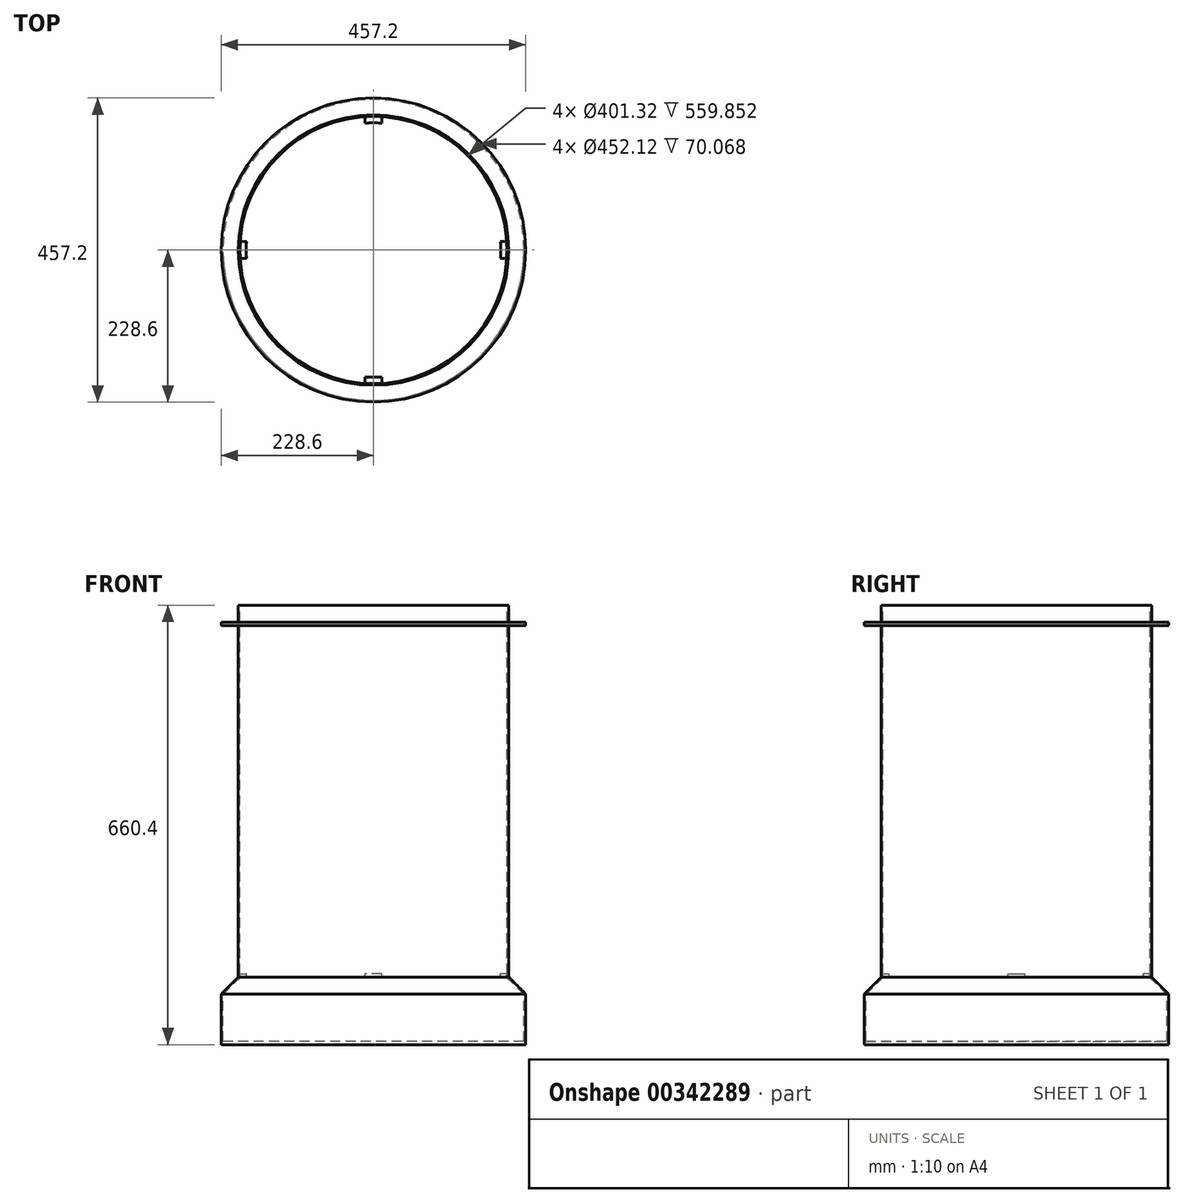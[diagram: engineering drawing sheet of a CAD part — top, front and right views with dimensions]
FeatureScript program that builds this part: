
annotation { "Feature Type Name" : "Feature", "Feature Type Description" : "" }
export const myFeature = defineFeature(function(context is Context, id is Id, definition is map)
    precondition{}
    {
        {
            var Q0;
            Q0=qCreatedBy(makeId("Front.planeOp"),FACE);
            var sketch = newSketch(context, id + "F0", { "sketchPlane" : qUnion([Q0])});
            skLineSegment(sketch, "E0", {"start": v(0, 0) * mm, "end": v(228.6, 0) * mm});
            skLineSegment(sketch, "E1", {"start": v(228.6, 0) * mm, "end": v(228.6, 76.2) * mm});
            skLineSegment(sketch, "E2", {"start": v(228.6, 76.2) * mm, "end": v(203.2, 101.6) * mm});
            skLineSegment(sketch, "E3", {"start": v(203.2, 101.6) * mm, "end": v(203.2, 629.92) * mm});
            skLineSegment(sketch, "E4", {"start": v(203.2, 629.92) * mm, "end": v(228.6, 629.92) * mm});
            skLineSegment(sketch, "E5", {"start": v(228.6, 629.92) * mm, "end": v(228.6, 635) * mm});
            skLineSegment(sketch, "E6", {"start": v(228.6, 635) * mm, "end": v(203.2, 635) * mm});
            skLineSegment(sketch, "E7", {"start": v(203.2, 635) * mm, "end": v(203.2, 660.4) * mm});
            skLineSegment(sketch, "E8", {"start": v(203.2, 660.4) * mm, "end": v(200.66, 660.4) * mm});
            skLineSegment(sketch, "E9", {"start": v(200.66, 660.4) * mm, "end": v(200.66, 106.68) * mm});
            skLineSegment(sketch, "E10", {"start": v(200.66, 106.68) * mm, "end": v(191.14, 106.68) * mm});
            skLineSegment(sketch, "E11", {"start": v(191.14, 106.68) * mm, "end": v(191.14, 101.6) * mm});
            skLineSegment(sketch, "E12", {"start": v(191.14, 101.6) * mm, "end": v(199.6, 101.6) * mm});
            skLineSegment(sketch, "E13", {"start": v(199.6, 101.6) * mm, "end": v(226.06, 75.15) * mm});
            skLineSegment(sketch, "E14", {"start": v(226.06, 75.15) * mm, "end": v(226.06, 5.08) * mm});
            skLineSegment(sketch, "E15", {"start": v(226.06, 5.08) * mm, "end": v(0, 5.08) * mm});
            skLineSegment(sketch, "E16", {"start": v(0, 5.08) * mm, "end": v(0, 0) * mm});
            skSolve(sketch);
        }
        {
            var Q0;
            Q0 = qSketchRegion(id + "F0", true);
            var Q1;
            Q1=sQuery(id+"F0.wireOp",EDGE,"E16");
            revolve(context, id + "F1", {"entities" : qUnion([Q0]), "axis" : qUnion([Q1]), "revolveType" : RevolveType.FULL});
        }
        {
            var Q0;
            Q0=makeQuery(id+"F1.opRevolve","SWEPT_FACE",FACE,{"disambiguationData":[OSD([sQuery(id+"F0.wireOp",EDGE,"E10")])]});
            var sketch = newSketch(context, id + "F2", { "sketchPlane" : qUnion([Q0])});
            skLineSegment(sketch, "E17", {"start": v(0, 200.66) * mm, "end": v(0, 0) * mm, "construction": true});
            skLineSegment(sketch, "E18", {"start": v(0, 0) * mm, "end": v(-200.66, 0) * mm, "construction": true});
            skLineSegment(sketch, "E19", {"start": v(-200.26, 12.7) * mm, "end": v(-190.71, 12.7) * mm});
            skLineSegment(sketch, "E20", {"start": v(-12.7, 200.26) * mm, "end": v(-12.7, 190.71) * mm});
            skArc(sketch, "E21", {"start": v(-12.7, 190.71) * mm, "mid": v(-135.15, 135.15) * mm, "end": v(-190.71, 12.7) * mm});
            skArc(sketch, "E22", {"start": v(-12.7, 200.26) * mm, "mid": v(-141.89, 141.89) * mm, "end": v(-200.26, 12.7) * mm});
            skArc(sketch, "E23.1.0", {"start": v(-190.71, -12.7) * mm, "mid": v(-135.15, -135.15) * mm, "end": v(-12.7, -190.71) * mm});
            skLineSegment(sketch, "E23.1.1", {"start": v(-200.26, -12.7) * mm, "end": v(-190.71, -12.7) * mm});
            skArc(sketch, "E23.1.2", {"start": v(-200.26, -12.7) * mm, "mid": v(-141.89, -141.89) * mm, "end": v(-12.7, -200.26) * mm});
            skLineSegment(sketch, "E23.1.3", {"start": v(-12.7, -200.26) * mm, "end": v(-12.7, -190.71) * mm});
            skArc(sketch, "E23.2.0", {"start": v(12.7, -190.71) * mm, "mid": v(135.15, -135.15) * mm, "end": v(190.71, -12.7) * mm});
            skLineSegment(sketch, "E23.2.1", {"start": v(12.7, -200.26) * mm, "end": v(12.7, -190.71) * mm});
            skArc(sketch, "E23.2.2", {"start": v(12.7, -200.26) * mm, "mid": v(141.89, -141.89) * mm, "end": v(200.26, -12.7) * mm});
            skLineSegment(sketch, "E23.2.3", {"start": v(200.26, -12.7) * mm, "end": v(190.71, -12.7) * mm});
            skArc(sketch, "E23.3.0", {"start": v(190.71, 12.7) * mm, "mid": v(135.15, 135.15) * mm, "end": v(12.7, 190.71) * mm});
            skLineSegment(sketch, "E23.3.1", {"start": v(200.26, 12.7) * mm, "end": v(190.71, 12.7) * mm});
            skArc(sketch, "E23.3.2", {"start": v(200.26, 12.7) * mm, "mid": v(141.89, 141.89) * mm, "end": v(12.7, 200.26) * mm});
            skLineSegment(sketch, "E23.3.3", {"start": v(12.7, 200.26) * mm, "end": v(12.7, 190.71) * mm});
            skSolve(sketch);
        }
        {
            var Q0;
            Q0 = qSketchRegion(id + "F2", true);
            extrude(context, id + "F3", {"entities" : qUnion([Q0]), "operationType" : NewBodyOperationType.REMOVE, "endBound" : BoundingType.UP_TO_NEXT, "oppositeDirection" : true, "depth" : 25.4 * mm, "offsetDistance" : 25.4 * mm});
        }
    });
